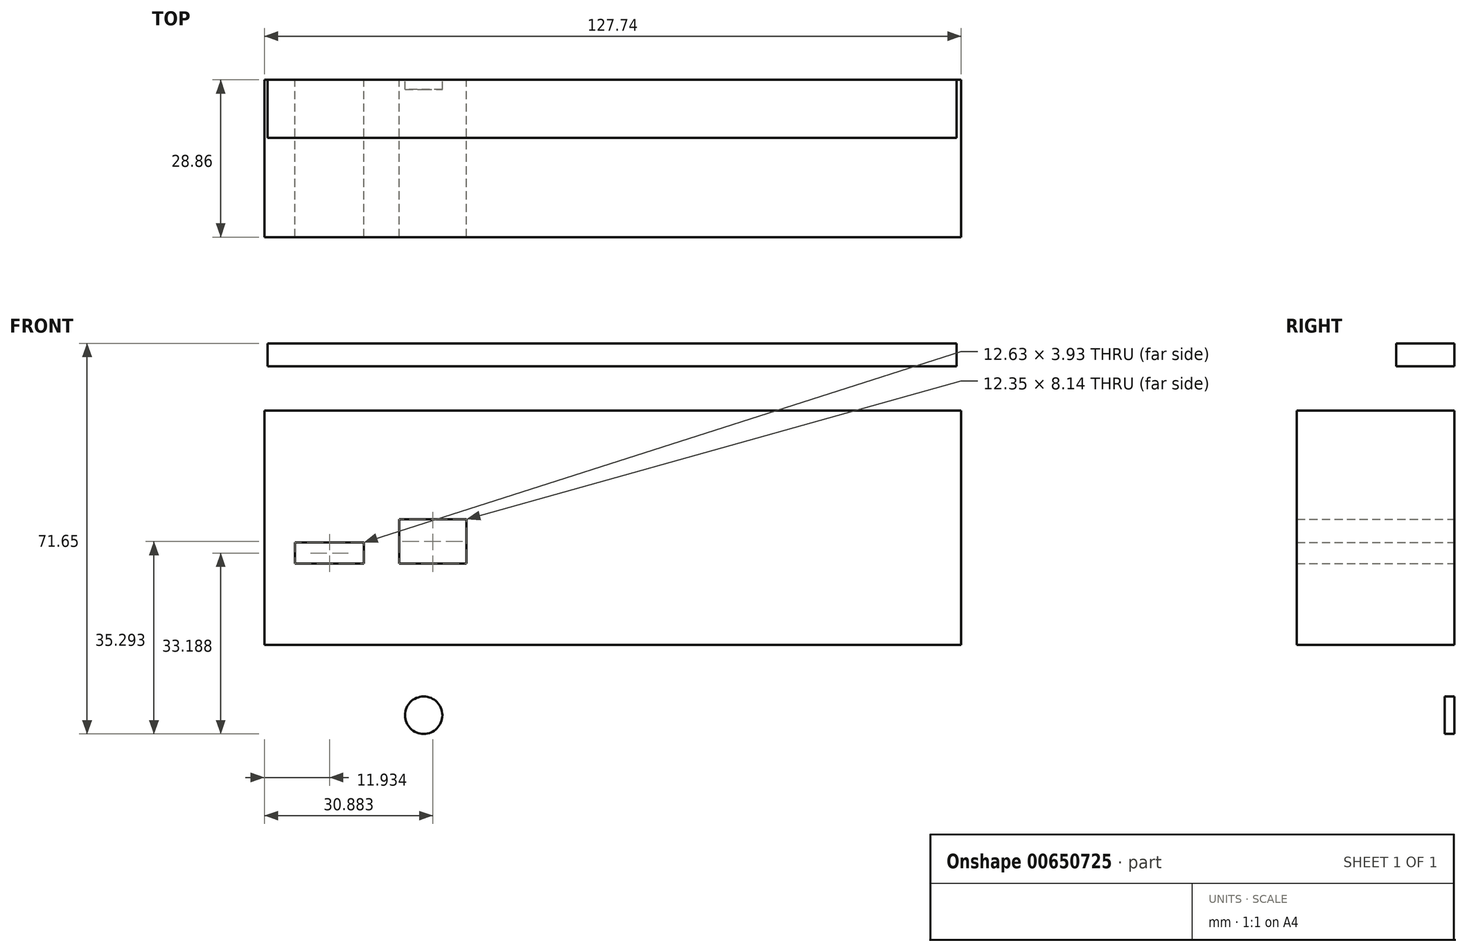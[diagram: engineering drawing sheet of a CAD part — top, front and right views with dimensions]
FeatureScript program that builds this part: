
annotation { "Feature Type Name" : "Feature", "Feature Type Description" : "" }
export const myFeature = defineFeature(function(context is Context, id is Id, definition is map)
    precondition{}
    {
        {
            var Q0;
            Q0=qCreatedBy(makeId("Front.planeOp"),FACE);
            var sketch = newSketch(context, id + "F0", { "sketchPlane" : qUnion([Q0])});
            skLineSegment(sketch, "E0.bottom", {"start": v(-63.87, 21.48) * mm, "end": v(63.87, 21.48) * mm});
            skLineSegment(sketch, "E0.top", {"start": v(-63.87, -21.48) * mm, "end": v(63.87, -21.48) * mm});
            skLineSegment(sketch, "E0.left", {"start": v(-63.87, 21.48) * mm, "end": v(-63.87, -21.48) * mm});
            skLineSegment(sketch, "E0.right", {"start": v(63.87, 21.48) * mm, "end": v(63.87, -21.48) * mm});
            skPoint(sketch, "E0.middle", {"position": v(0, 0) * mm});
            skLineSegment(sketch, "E1", {"start": v(-58.25, -6.6) * mm, "end": v(-45.62, -6.6) * mm});
            skLineSegment(sketch, "E2.top", {"start": v(-58.25, -2.67) * mm, "end": v(-45.62, -2.67) * mm});
            skLineSegment(sketch, "E2.left", {"start": v(-58.25, -6.6) * mm, "end": v(-58.25, -2.67) * mm});
            skLineSegment(sketch, "E2.right", {"start": v(-45.62, -6.6) * mm, "end": v(-45.62, -2.67) * mm});
            skLineSegment(sketch, "E3.bottom", {"start": v(-39.16, -6.6) * mm, "end": v(-26.81, -6.6) * mm});
            skLineSegment(sketch, "E3.top", {"start": v(-39.16, 1.54) * mm, "end": v(-26.81, 1.54) * mm});
            skLineSegment(sketch, "E3.left", {"start": v(-39.16, -6.6) * mm, "end": v(-39.16, 1.54) * mm});
            skLineSegment(sketch, "E3.right", {"start": v(-26.81, -6.6) * mm, "end": v(-26.81, 1.54) * mm});
            skSolve(sketch);
        }
        {
            var Q0;
            Q0 = qSketchRegion(id + "F0", true);
            extrude(context, id + "F1", {"entities" : qUnion([Q0]), "depth" : 10.16 * mm, "offsetDistance" : 25.4 * mm});
        }
        {
            var Q0;
            Q0=qCreatedBy(makeId("Front.planeOp"),FACE);
            var sketch = newSketch(context, id + "F2", { "sketchPlane" : qUnion([Q0])});
            skLineSegment(sketch, "E4.bottom", {"start": v(-63.3, 29.62) * mm, "end": v(63.03, 29.62) * mm});
            skLineSegment(sketch, "E4.top", {"start": v(-63.3, 33.83) * mm, "end": v(63.03, 33.83) * mm});
            skLineSegment(sketch, "E4.left", {"start": v(-63.3, 29.62) * mm, "end": v(-63.3, 33.83) * mm});
            skLineSegment(sketch, "E4.right", {"start": v(63.03, 29.62) * mm, "end": v(63.03, 33.83) * mm});
            skSolve(sketch);
        }
        {
            var Q0;
            Q0=makeQuery(id+"F2.imprint","IMPRINT",FACE,{"disambiguationData":[TD([[makeQuery(id+"F2.imprint","IMPRINT",EDGE,{"derivedFrom":sQuery(id+"F2.wireOp",EDGE,"E4.bottom")}),1.0]])]});
            extrude(context, id + "F3", {"entities" : qUnion([Q0]), "depth" : 10.67 * mm, "offsetDistance" : 25.4 * mm});
        }
        {
            var Q0;
            Q0=qCreatedBy(makeId("Front.planeOp"),FACE);
            var sketch = newSketch(context, id + "F4", { "sketchPlane" : qUnion([Q0])});
            skCircle(sketch, "E5", {"center": v(-34.67, -34.4) * mm, "radius": 3.43 * mm});
            skSolve(sketch);
        }
        {
            var Q0;
            Q0 = qSketchRegion(id + "F4", true);
            extrude(context, id + "F5", {"entities" : qUnion([Q0]), "depth" : 1.78 * mm, "offsetDistance" : 25.4 * mm});
        }
        {
            var Q0;
            Q0=makeQuery(id+"F1.opExtrude","SWEPT_FACE",FACE,{"disambiguationData":[OSD([sQuery(id+"F0.wireOp",EDGE,"E0.right")])]});
            extrude(context, id + "F6", {"entities" : qUnion([Q0]), "operationType" : NewBodyOperationType.ADD, "oppositeDirection" : true, "depth" : 3.52 * mm, "offsetDistance" : 25.4 * mm});
        }
        {
            var Q0;
            Q0=makeQuery(id+"F1.opExtrude","CAP_FACE",FACE,{"disambiguationData":[OSD([sQuery(id+"F0.wireOp",EDGE,"E0.bottom"),sQuery(id+"F0.wireOp",EDGE,"E0.top"),sQuery(id+"F0.wireOp",EDGE,"E0.left"),sQuery(id+"F0.wireOp",EDGE,"E0.right"),sQuery(id+"F0.wireOp",EDGE,"E1"),sQuery(id+"F0.wireOp",EDGE,"E2.top"),sQuery(id+"F0.wireOp",EDGE,"E2.left"),sQuery(id+"F0.wireOp",EDGE,"E2.right"),sQuery(id+"F0.wireOp",EDGE,"E3.top"),sQuery(id+"F0.wireOp",EDGE,"E3.left"),sQuery(id+"F0.wireOp",EDGE,"E3.right"),sQuery(id+"F0.wireOp",EDGE,"E3.bottom")])],"isStart":true});
            extrude(context, id + "F7", {"entities" : qUnion([Q0]), "operationType" : NewBodyOperationType.ADD, "oppositeDirection" : true, "depth" : 28.86 * mm, "offsetDistance" : 25.4 * mm});
        }
    });
